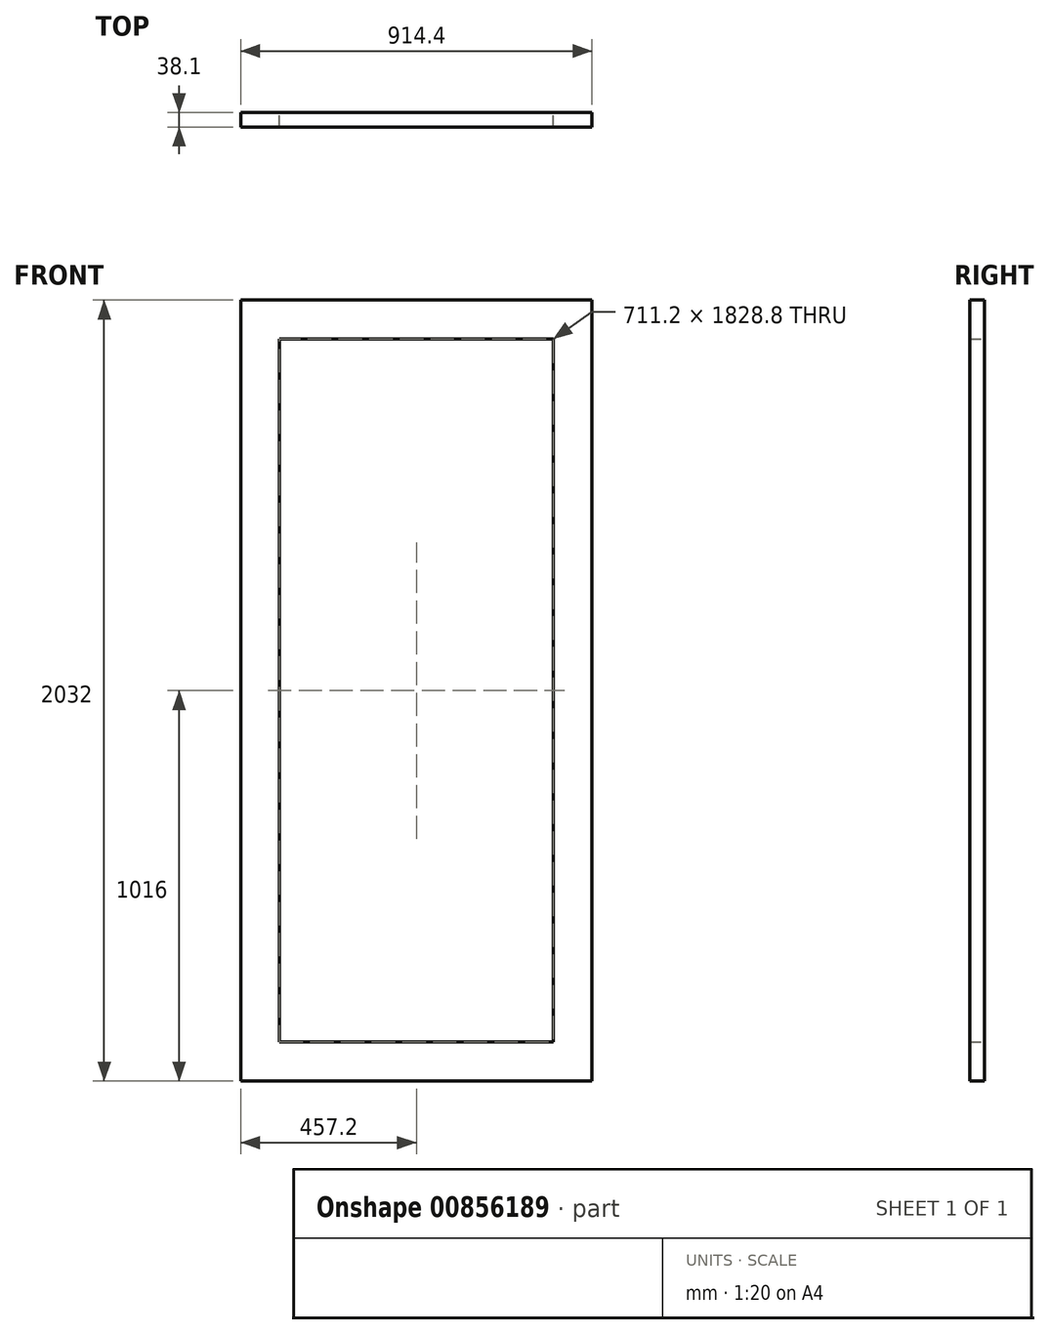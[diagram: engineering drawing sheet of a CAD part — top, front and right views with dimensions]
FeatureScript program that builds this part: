
annotation { "Feature Type Name" : "Feature", "Feature Type Description" : "" }
export const myFeature = defineFeature(function(context is Context, id is Id, definition is map)
    precondition{}
    {
        {
            var Q0;
            Q0=qCreatedBy(makeId("Front.planeOp"),FACE);
            var sketch = newSketch(context, id + "F0", { "sketchPlane" : qUnion([Q0])});
            skLineSegment(sketch, "E0.bottom", {"start": v(0, 0) * mm, "end": v(-914.4, 0) * mm});
            skLineSegment(sketch, "E0.top", {"start": v(0, 2032) * mm, "end": v(-914.4, 2032) * mm});
            skLineSegment(sketch, "E0.left", {"start": v(0, 0) * mm, "end": v(0, 2032) * mm});
            skLineSegment(sketch, "E0.right", {"start": v(-914.4, 0) * mm, "end": v(-914.4, 2032) * mm});
            skLineSegment(sketch, "E1.bottom", {"start": v(-812.8, 1930.4) * mm, "end": v(-101.6, 1930.4) * mm});
            skLineSegment(sketch, "E1.top", {"start": v(-812.8, 101.6) * mm, "end": v(-101.6, 101.6) * mm});
            skLineSegment(sketch, "E1.left", {"start": v(-812.8, 1930.4) * mm, "end": v(-812.8, 101.6) * mm});
            skLineSegment(sketch, "E1.right", {"start": v(-101.6, 1930.4) * mm, "end": v(-101.6, 101.6) * mm});
            skSolve(sketch);
        }
        {
            var Q0;
            Q0=makeQuery(id+"F0.imprint","IMPRINT",FACE,{"disambiguationData":[TD([[makeQuery(id+"F0.imprint","IMPRINT",EDGE,{"derivedFrom":sQuery(id+"F0.wireOp",EDGE,"E0.bottom")}),-1.0]])]});
            extrude(context, id + "F1", {"entities" : qUnion([Q0]), "depth" : 38.1 * mm, "offsetDistance" : 30.48 * mm});
        }
    });
